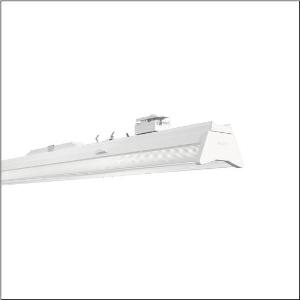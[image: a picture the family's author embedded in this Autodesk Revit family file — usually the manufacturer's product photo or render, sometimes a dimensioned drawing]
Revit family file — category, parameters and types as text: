
# Revit family: licross_r__21_performance_mo_52tm16dn445g_a9c4
name_source: partatom
category: Lighting Fixtures
units: mm (PartAtom-declared; Revit-internal decimal feet)

## family parameters
Cut with Voids When Loaded = No
Host = Face
Light Source = No
Part Type = Normal
Room Calculation Point = No
Round Connector Dimension = Use Diameter
Shared = No

## types (1)
- --- (1 x LED, 4500 lm, 24.9 W, 4000K)
    Apparent Load = 25 VA
    CIE Flux Codes = 66 88 96 79 100
    Color Rendering = 80
    Color Temperature = 4000K
    Default Elevation = 1800 mm
    Description = Licross® 21 Performance MO, luminaire insert, of sheet steel, galvanised, coil coated, white, length: 1.500mm, width: 120mm, height: 123mm, LED rated luminous flux: 4.500lm, light colour: 840, SDCM (Standard Deviation of Colour Matching)MacAdam ≤ 3 SDCM (initial), control gear: DALI 2, with plug, 5-pole, with phase selection, mains connection: 220..240V, AC, 50/60Hz, rated input power: 25W, internal wiring halogen-free, primary light control with lens, of plastic, primary optical cover: cover, of PMMA, CAT 2 (L<= 3000cd/m²), light emission: direct/indirect distribution, primary light characteristic: symmetric, protection rating (complete): IP40, insulation class (complete): insulation class I (protective earthing), certification: CE, ENEC, UKCA, protection symbol: D if used in an environment without relevant dust loads with corresponding accessories, impact resistance: IK06, permissible ambient temperature for indoor applications: -25..+50°C, corresponds to IFS (International Featured Standards) requirements for safety and quality in the food industry, reducing of maximum allowable ambient temperature of 5°C with ceiling mounting, LABS conformity tested according to VDMA 24364:2018-05, packaging unit: 1 piece
    Height = 114 mm
    Lamp = 1 x LED
    Lamp Light Flux = 4500 lm
    Lamp Power = 24.9 W
    Lamp count = 1
    Length = 1500 mm
    Luminous efficacy = 181 lm/W
    Manufacturer = Siteco
    ModVariant = No
    Model = 52TM16DN445G
    Mounting Place = Ceiling
    Mounting Type = Pendant
    Number of Poles = 1
    OnlyDefault = Yes
    Power Factor = 1
    Product Name = Licross® 21 Performance MO
    Product group = luminaire insert | ceiling pendant
    ProductGroupID = 901
    Protection Class = Protection class I
    Protection Degree = IP 40
    RLX_Detail_Level = 1
    RLX_Emergency_Light_Flux = 0 lm
    RLX_Emergency_Type = 0
    RLX_Emergency_Type_DB = No
    RlxData = <blob elided: 33693 chars, md5=9871f7e1>
    Socket = socket
    Standby Power = 0 W
    System Light Flux = 4500 lm
    System Power = 25 W
    Type Comments = factory setting: luminous flux: 100 % | dim-lin: 254 | 165 mA
    Type Image = l_1256138.jpg
    URL = http://relux.com
    VarID = @adj_058783
    Voltage = 0 V
    Weight = 0.00 kg
    Width = 120 mm

## geometry (parser evidence)
native form markers: Blend x4, Sweep x11
no freeform markers — native parametric forms only
